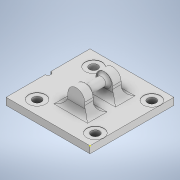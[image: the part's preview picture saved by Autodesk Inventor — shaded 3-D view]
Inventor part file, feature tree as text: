
AUTODESK INVENTOR PART (.ipt)
format: ipt  version: 2022 (Build 260153000, 153)  size: 218,624 bytes
history: native  units: in
note: dims shown in document units (in); Inventor stores cm internally (conversion verified against a paired STEP export)
features: sketch x6, extrude x4, fillet x3, hole x1
ambient origin geometry x8: Origin, YZ Plane, XZ Plane, XY Plane, X Axis, Y Axis, Z Axis, Center Point
bodies: Solid1 (feature_tree)
feature tree (14):
  extrude  "Extrusion1"  Depth=1.1811in
  hole  "Hole1"  [1 undecoded]
  extrude  "Extrusion2"  Depth=0.7953in
  extrude  "Extrusion3"  Depth=0.1929in
  fillet  "Fillet1"  Radius=0.7953in
  extrude  "Extrusion4"  Depth=0.0787in
  fillet  "Fillet2"  Radius=0.1929in
  fillet  "Fillet3"  Radius=0.1929in
  sketch  "Sketch6"  dims[d18=0.1181in d19=0.8189in d20=0.1929in d21=0.1929in d22=0.2362in d23=0.1181in d24=0.3346in d25=0.4094in d26=0.1181in d27=0.2756in d28=0.5354in d29=0.4094in d30=0.2756in d31=0.0in d32=0.1181in d33=0.1181in d34=0.1772in d35=0.1181in d36=0.1969in d37=0.0in d38=0.0394in d39=0.0787in]
  sketch  "Sketch1"  dims[d0=1.1811in d1=1.1811in]
  sketch  "Sketch2"  dims[d2=0.0984in d3=0.0in]
  sketch  "Sketch3"  dims[d4=0.1181in d5=0.2362in d6=0.2362in d7=0.0039in d8=90.0deg d9=0.315in d10=0.8108in d11=0.0787in]
  sketch  "Sketch4"  dims[d12=0.0394in d13=0.0in d14=0.7953in]
  sketch  "Sketch5"  dims[d15=0.8189in d16=0.1929in d17=0.7953in]
note: 1 required parameter value undecoded (feature->parameter linkage not recoverable at this tier; creation-order binding heuristic only, values carry confidence <= 0.55)
